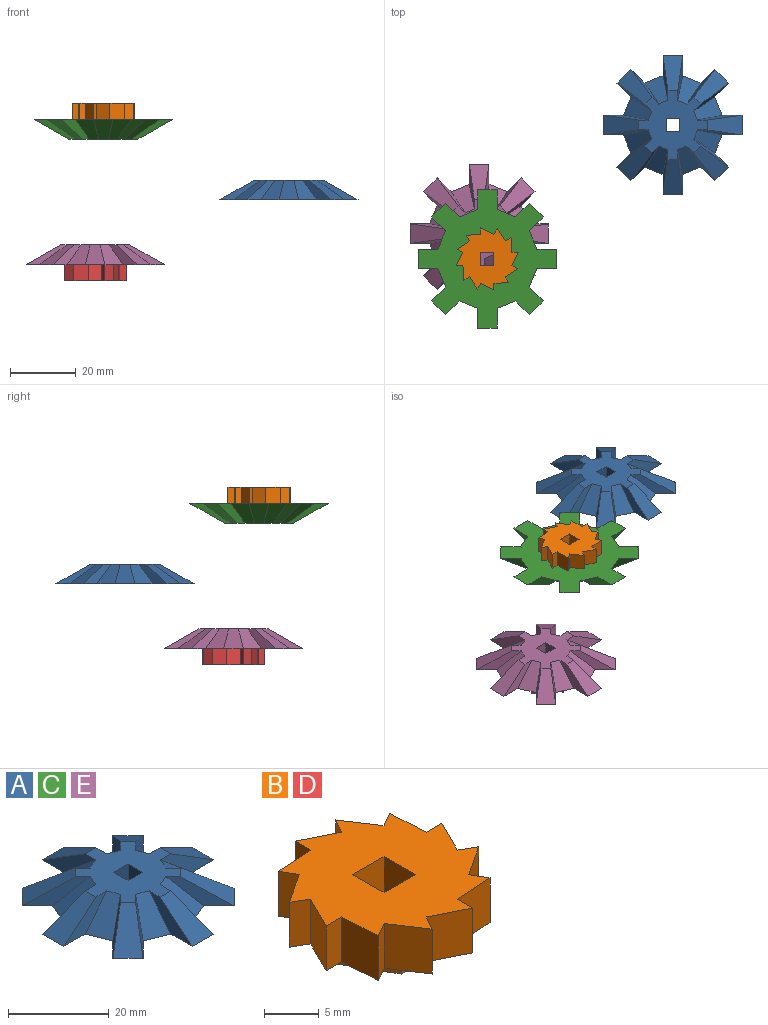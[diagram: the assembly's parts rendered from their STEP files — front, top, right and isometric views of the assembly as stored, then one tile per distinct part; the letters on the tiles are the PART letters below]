
ASSEMBLY  parts=5 mates=6
PART A: 45 faces, bbox 42.2x42.2x6 mm
  f0: plane 4x4mm, normal (0,-1,0), area 16mm2, adj f1,f2,f5,f38
  f1: plane 4x4mm, normal (-1,0,0), area 16mm2, adj f0,f3,f5,f38
  f2: plane 4x4mm, normal (1,0,0), area 16mm2, adj f0,f3,f5,f38
  f3: plane 4x4mm, normal (0,1,0), area 16mm2, adj f1,f2,f5,f38
  f4: plane 42.16x42.16mm, normal (0,0,-1), area 918.4mm2, adj f6,f7,f8,f9,f10,f11,f12,f13
  f5: plane 21.08x21.08mm, normal (0,0,1), area 237mm2, adj f0,f1,f2,f3,f6,f7,f8,f9
  f6: plane 13.54x6mm, normal (0.97,0,0.24), area 27.8mm2, adj f4,f5,f7,f37
  f7: plane 10.54x6mm, normal (0,0.49,0.87), area 54.6mm2, adj f4,f5,f6,f8
  f8: plane 13.54x6mm, normal (-0.97,0,0.24), area 27.8mm2, adj f4,f5,f7,f9
  f9: plane 8.69x7.04mm, normal (-0.24,0.58,0.78), area 43.4mm2, adj f4,f5,f8,f10
  f10: plane 10.64x8.51mm, normal (0.69,0.69,0.24), area 27.8mm2, adj f4,f5,f9,f11
  f11: plane 10.64x10.64mm, normal (-0.35,0.35,0.87), area 54.6mm2, adj f4,f5,f10,f12
  f12: plane 10.64x8.51mm, normal (-0.69,-0.69,0.24), area 27.8mm2, adj f4,f5,f11,f13
  f13: plane 8.69x7.04mm, normal (-0.58,0.24,0.78), area 43.4mm2, adj f4,f5,f12,f14
  f14: plane 13.54x6mm, normal (0,0.97,0.24), area 27.8mm2, adj f4,f5,f13,f15
  f15: plane 10.54x6mm, normal (-0.49,0,0.87), area 54.6mm2, adj f4,f5,f14,f16
  f16: plane 13.54x6mm, normal (0,-0.97,0.24), area 27.8mm2, adj f4,f5,f15,f17
  f17: plane 8.69x7.04mm, normal (-0.58,-0.24,0.78), area 43.4mm2, adj f4,f5,f16,f18
  f18: plane 10.64x8.51mm, normal (-0.69,0.69,0.24), area 27.8mm2, adj f4,f5,f17,f19
  f19: plane 10.64x10.64mm, normal (-0.35,-0.35,0.87), area 54.6mm2, adj f4,f5,f18,f20
  f20: plane 10.64x8.51mm, normal (0.69,-0.69,0.24), area 27.8mm2, adj f4,f5,f19,f21
  f21: plane 8.69x7.04mm, normal (-0.24,-0.58,0.78), area 43.4mm2, adj f4,f5,f20,f22
  f22: plane 13.54x6mm, normal (-0.97,0,0.24), area 27.8mm2, adj f4,f5,f21,f23
  f23: plane 10.54x6mm, normal (0,-0.49,0.87), area 54.6mm2, adj f4,f5,f22,f24
  f24: plane 13.54x6mm, normal (0.97,0,0.24), area 27.8mm2, adj f4,f5,f23,f25
  f25: plane 8.69x7.04mm, normal (0.24,-0.58,0.78), area 43.4mm2, adj f4,f5,f24,f26
  f26: plane 10.64x8.51mm, normal (-0.69,-0.69,0.24), area 27.8mm2, adj f4,f5,f25,f27
  f27: plane 10.64x10.64mm, normal (0.35,-0.35,0.87), area 54.6mm2, adj f4,f5,f26,f28
  f28: plane 10.64x8.51mm, normal (0.69,0.69,0.24), area 27.8mm2, adj f4,f5,f27,f29
  f29: plane 8.69x7.04mm, normal (0.58,-0.24,0.78), area 43.4mm2, adj f4,f5,f28,f30
  f30: plane 13.54x6mm, normal (0,-0.97,0.24), area 27.8mm2, adj f4,f5,f29,f31
  f31: plane 10.54x6mm, normal (0.49,0,0.87), area 54.6mm2, adj f4,f5,f30,f32
  f32: plane 13.54x6mm, normal (0,0.97,0.24), area 27.8mm2, adj f4,f5,f31,f33
  f33: plane 8.69x7.04mm, normal (0.58,0.24,0.78), area 43.4mm2, adj f4,f5,f32,f34
  f34: plane 10.64x8.51mm, normal (0.69,-0.69,0.24), area 27.8mm2, adj f4,f5,f33,f35
  f35: plane 10.64x10.64mm, normal (0.35,0.35,0.87), area 54.6mm2, adj f4,f5,f34,f36
  f36: plane 10.64x8.51mm, normal (-0.69,0.69,0.24), area 27.8mm2, adj f4,f5,f35,f37
  f37: plane 8.69x7.04mm, normal (0.24,0.58,0.78), area 43.4mm2, adj f4,f5,f6,f36
  f38: plane 12x10.39mm, normal (0,0,-1), area 77.5mm2, adj f0,f1,f2,f3,f39,f40,f41,f42
  f39: plane 5.2x3mm, normal (0.87,-0.5,0), area 12mm2, adj f4,f38,f40,f44
  f40: plane 6x2mm, normal (0,-1,0), area 12mm2, adj f4,f38,f39,f41
  f41: plane 5.2x3mm, normal (-0.87,-0.5,0), area 12mm2, adj f4,f38,f40,f42
  f42: plane 5.2x3mm, normal (-0.87,0.5,0), area 12mm2, adj f4,f38,f41,f43
  f43: plane 6x2mm, normal (0,1,0), area 12mm2, adj f4,f38,f42,f44
  f44: plane 5.2x3mm, normal (0.87,0.5,0), area 12mm2, adj f4,f38,f39,f43
PART B: 37 faces, bbox 18.9x18.9x7 mm
  f0: plane 5.2x3mm, normal (0.87,0.5,0), area 12mm2, adj f1,f5,f6,f7
  f1: plane 6x2mm, normal (0,1,0), area 12mm2, adj f0,f2,f6,f7
  f2: plane 5.2x3mm, normal (-0.87,0.5,0), area 12mm2, adj f1,f3,f6,f7
  f3: plane 5.2x3mm, normal (-0.87,-0.5,0), area 12mm2, adj f2,f4,f6,f7
  f4: plane 6x2mm, normal (0,-1,0), area 12mm2, adj f3,f5,f6,f7
  f5: plane 5.2x3mm, normal (0.87,-0.5,0), area 12mm2, adj f0,f4,f6,f7
  f6: plane 12x10.39mm, normal (0,0,-1), area 77.5mm2, adj f0,f1,f2,f3,f4,f5,f33,f34
  f7: plane 18.93x18.93mm, normal (0,0,-1), area 133.6mm2, adj f0,f1,f2,f3,f4,f5,f8,f9
  f8: plane 5x2mm, normal (-1,0,0), area 10mm2, adj f7,f9,f31,f32
  f9: plane 5x4.46mm, normal (-0.06,1,0), area 22.4mm2, adj f7,f8,f10,f32
  f10: plane 5x1.73mm, normal (-0.87,-0.5,0), area 10mm2, adj f7,f9,f11,f32
  f11: plane 5x3.73mm, normal (-0.55,0.83,0), area 22.4mm2, adj f7,f10,f12,f32
  f12: plane 5x1.73mm, normal (-0.5,-0.87,0), area 10mm2, adj f7,f11,f13,f32
  f13: plane 5x4mm, normal (-0.89,0.45,0), area 22.4mm2, adj f7,f12,f14,f32
  f14: plane 5x2mm, normal (0,-1,0), area 10mm2, adj f7,f13,f15,f32
  f15: plane 5x4.46mm, normal (-1,-0.06,0), area 22.4mm2, adj f7,f14,f16,f32
  f16: plane 5x1.73mm, normal (0.5,-0.87,0), area 10mm2, adj f7,f15,f17,f32
  f17: plane 5x3.73mm, normal (-0.83,-0.55,0), area 22.4mm2, adj f7,f16,f18,f32
  f18: plane 5x1.73mm, normal (0.87,-0.5,0), area 10mm2, adj f7,f17,f19,f32
  f19: plane 5x4mm, normal (-0.45,-0.89,0), area 22.4mm2, adj f7,f18,f20,f32
  f20: plane 5x2mm, normal (1,0,0), area 10mm2, adj f7,f19,f21,f32
  f21: plane 5x4.46mm, normal (0.06,-1,0), area 22.4mm2, adj f7,f20,f22,f32
  f22: plane 5x1.73mm, normal (0.87,0.5,0), area 10mm2, adj f7,f21,f23,f32
  f23: plane 5x3.73mm, normal (0.55,-0.83,0), area 22.4mm2, adj f7,f22,f24,f32
  f24: plane 5x1.73mm, normal (0.5,0.87,0), area 10mm2, adj f7,f23,f25,f32
  f25: plane 5x4mm, normal (0.89,-0.45,0), area 22.4mm2, adj f7,f24,f26,f32
  f26: plane 5x2mm, normal (0,1,0), area 10mm2, adj f7,f25,f27,f32
  f27: plane 5x4.46mm, normal (1,0.06,0), area 22.4mm2, adj f7,f26,f28,f32
  f28: plane 5x1.73mm, normal (-0.5,0.87,0), area 10mm2, adj f7,f27,f29,f32
  f29: plane 5x3.73mm, normal (0.83,0.55,0), area 22.4mm2, adj f7,f28,f30,f32
  f30: plane 5x1.73mm, normal (-0.87,0.5,0), area 10mm2, adj f7,f29,f31,f32
  f31: plane 5x4mm, normal (0.45,0.89,0), area 22.4mm2, adj f7,f8,f30,f32
  f32: plane 18.93x18.93mm, normal (0,0,1), area 211.1mm2, adj f8,f9,f10,f11,f12,f13,f14,f15
  f33: plane 7x4mm, normal (0,-1,0), area 28mm2, adj f6,f32,f34,f35
  f34: plane 7x4mm, normal (-1,0,0), area 28mm2, adj f6,f32,f33,f36
  f35: plane 7x4mm, normal (1,0,0), area 28mm2, adj f6,f32,f33,f36
  f36: plane 7x4mm, normal (0,1,0), area 28mm2, adj f6,f32,f34,f35
PART C: same geometry as A
PART D: same geometry as B
PART E: same geometry as A
PLACE A t=(25.22,5.92,-15.95)mm
PLACE B t=(-31.31,-34.93,6.55)mm
PLACE C rot(axis=(0,-1,0),180deg) t=(-31.31,-34.93,8.55)mm
PLACE D rot(axis=(0,1,0),180deg) t=(-33.82,-27.16,-33.69)mm
PLACE E rot(axis=(0,0,1),180deg) t=(-33.82,-27.16,-35.69)mm
MATE fastened C.f4 <-> B.f7  axis (0,0,1) through (-31.31,-34.93,8.55)mm
MATE parallel E.f4 <-> D.f6  axis (0,0,-1) through (-33.82,-27.16,-35.69)mm
MATE parallel C.f4 <-> B.f6  axis (0,0,1) through (-31.31,-34.93,8.55)mm
MATE parallel C.f5 <-> E.f5  axis (0,0,-1) through (-31.31,-36.93,2.55)mm
MATE parallel D.f35 <-> B.f34  axis (-1,0,0) through (-31.82,-27.16,-37.19)mm
MATE fastened D.f7 <-> E.f4  axis (0,0,1) through (-33.82,-27.16,-35.69)mm
